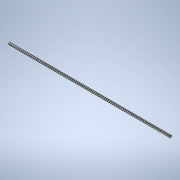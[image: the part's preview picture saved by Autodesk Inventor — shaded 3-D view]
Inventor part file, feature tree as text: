
AUTODESK INVENTOR PART (.ipt)
format: ipt  version: 2020.1 (Build 241239000, 239)  size: 100,864 bytes
history: native  units: mm
features: extrude x3, sketch x3
ambient origin geometry x8: Origin, YZ Plane, XZ Plane, XY Plane, X Axis, Y Axis, Z Axis, Center Point
bodies: Solid1 (feature_tree)
feature tree (6):
  extrude  "Extrusion1"  Depth=165.1mm TaperAngle=0.0deg
  extrude  "Extrusion2"  Depth=20.32mm TaperAngle=0.0deg
  extrude  "Extrusion3"  [1 undecoded]
  sketch  "Sketch1"  dims[d0=3.175mm d1=165.1mm d2=0.0mm]
  sketch  "Sketch2"  dims[d3=20.32mm d4=0.0mm d5=20.32mm d6=0.0mm]
  sketch  "Sketch3"
note: 1 required parameter value undecoded (feature->parameter linkage not recoverable at this tier; creation-order binding heuristic only, values carry confidence <= 0.55)
